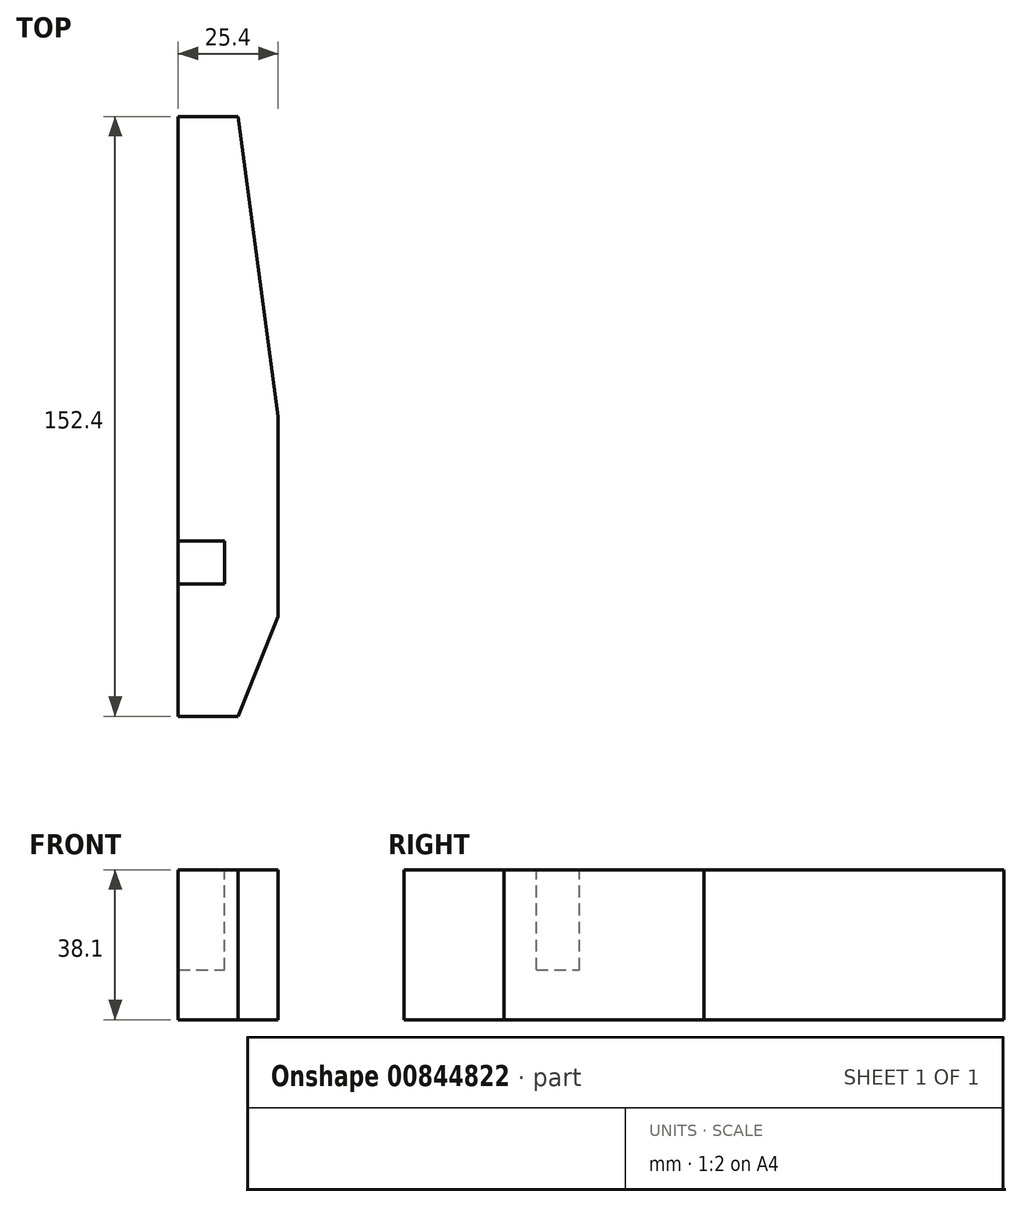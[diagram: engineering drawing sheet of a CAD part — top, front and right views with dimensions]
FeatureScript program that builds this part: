
annotation { "Feature Type Name" : "Feature", "Feature Type Description" : "" }
export const myFeature = defineFeature(function(context is Context, id is Id, definition is map)
    precondition{}
    {
        {
            var Q0;
            Q0=qCreatedBy(makeId("Right.planeOp"),FACE);
            var sketch = newSketch(context, id + "F0", { "sketchPlane" : qUnion([Q0])});
            skLineSegment(sketch, "E0.bottom", {"start": v(-114.3, 31.75) * mm, "end": v(38.1, 31.75) * mm});
            skLineSegment(sketch, "E0.top", {"start": v(-114.3, -6.35) * mm, "end": v(38.1, -6.35) * mm});
            skLineSegment(sketch, "E0.left", {"start": v(-114.3, 31.75) * mm, "end": v(-114.3, -6.35) * mm});
            skLineSegment(sketch, "E0.right", {"start": v(38.1, 31.75) * mm, "end": v(38.1, -6.35) * mm});
            skSolve(sketch);
        }
        {
            var Q0;
            Q0=makeQuery(id+"F0.imprint","IMPRINT",FACE,{"disambiguationData":[TD([[makeQuery(id+"F0.imprint","IMPRINT",EDGE,{"derivedFrom":sQuery(id+"F0.wireOp",EDGE,"E0.bottom")}),-1.0]])]});
            extrude(context, id + "F1", {"entities" : qUnion([Q0]), "endBound" : BoundingType.SYMMETRIC, "oppositeDirection" : true, "depth" : 25.4 * mm, "offsetDistance" : 25.4 * mm});
        }
        {
            var Q0;
            Q0=makeQuery(id+"F1.opExtrude","CAP_EDGE",EDGE,{"disambiguationData":[OSD([sQuery(id+"F0.wireOp",EDGE,"E0.left")])],"isStart":true});
            chamfer(context, id + "F2", {"entities" : qUnion([Q0]), "chamferType" : ChamferType.TWO_OFFSETS, "width1" : 25.4 * mm, "oppositeDirection" : false, "width2" : 10.16 * mm, "tangentPropagation" : true});
        }
        {
            var Q0;
            Q0=makeQuery(id+"F1.opExtrude","CAP_EDGE",EDGE,{"disambiguationData":[OSD([sQuery(id+"F0.wireOp",EDGE,"E0.right")])],"isStart":true});
            chamfer(context, id + "F3", {"entities" : qUnion([Q0]), "chamferType" : ChamferType.TWO_OFFSETS, "width1" : 76.2 * mm, "oppositeDirection" : true, "width2" : 10.16 * mm, "tangentPropagation" : true});
        }
        {
            var Q0;
            Q0=makeQuery(id+"F1.opExtrude","SWEPT_FACE",FACE,{"disambiguationData":[OSD([sQuery(id+"F0.wireOp",EDGE,"E0.bottom")])]});
            var sketch = newSketch(context, id + "F4", { "sketchPlane" : qUnion([Q0])});
            skLineSegment(sketch, "E1", {"start": v(-12.7, -80.73) * mm, "end": v(-0.86, -80.73) * mm});
            skLineSegment(sketch, "E2", {"start": v(-0.86, -80.73) * mm, "end": v(-0.86, -69.8) * mm});
            skLineSegment(sketch, "E3", {"start": v(-0.86, -69.8) * mm, "end": v(-12.7, -69.8) * mm});
            skLineSegment(sketch, "E4", {"start": v(-12.7, -80.73) * mm, "end": v(-12.7, -69.8) * mm});
            skSolve(sketch);
        }
        {
            var Q0;
            Q0=makeQuery(id+"F4.imprint","IMPRINT",FACE,{"disambiguationData":[TD([[makeQuery(id+"F4.imprint","IMPRINT",EDGE,{"derivedFrom":sQuery(id+"F4.wireOp",EDGE,"E1")}),1.0]])]});
            extrude(context, id + "F5", {"entities" : qUnion([Q0]), "operationType" : NewBodyOperationType.REMOVE, "oppositeDirection" : true, "depth" : 25.4 * mm, "offsetDistance" : 25.4 * mm});
        }
    });
